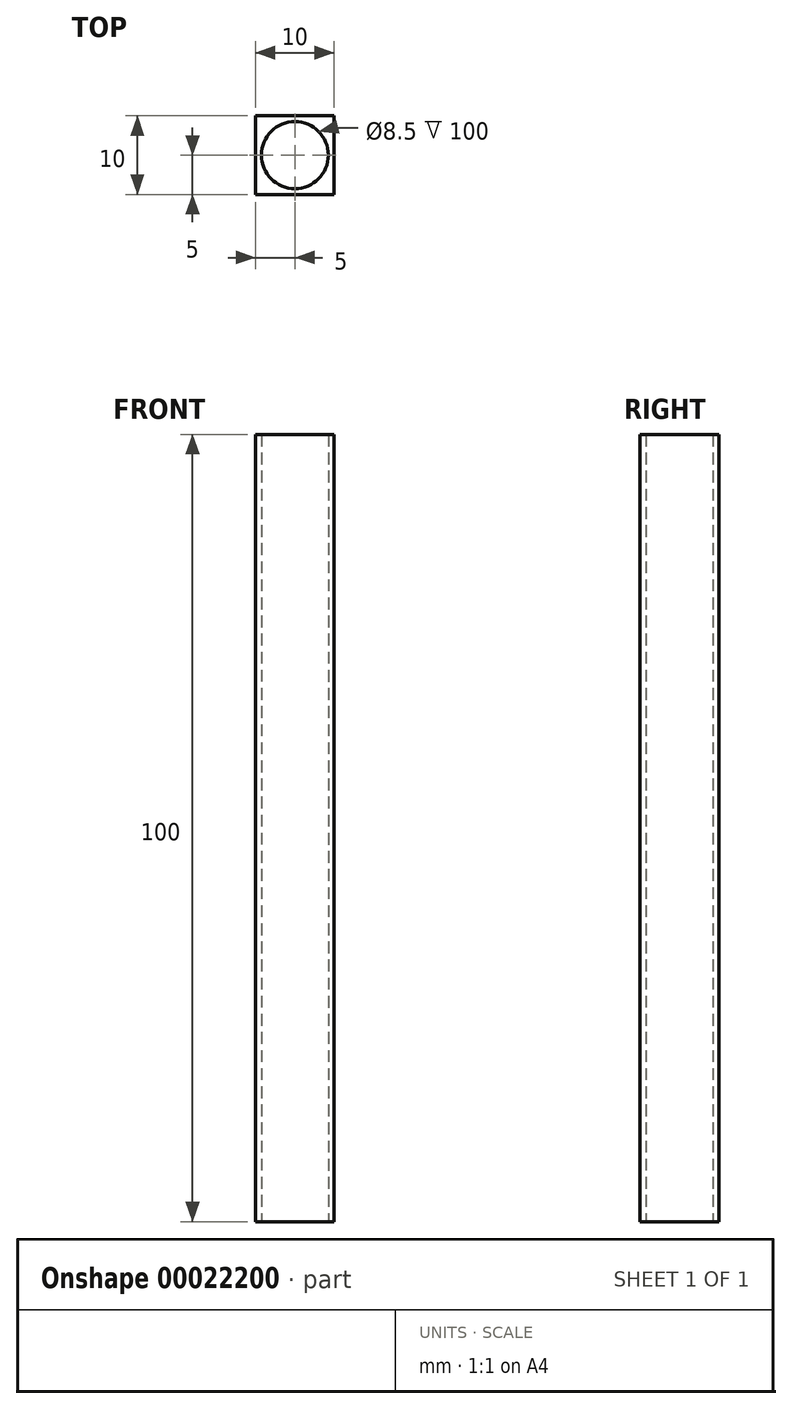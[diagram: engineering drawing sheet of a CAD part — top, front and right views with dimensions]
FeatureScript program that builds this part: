
annotation { "Feature Type Name" : "Feature", "Feature Type Description" : "" }
export const myFeature = defineFeature(function(context is Context, id is Id, definition is map)
    precondition{}
    {
        {
            var Q0;
            Q0=qCreatedBy(makeId("Top.planeOp"),FACE);
            var sketch = newSketch(context, id + "F0", { "sketchPlane" : qUnion([Q0])});
            skLineSegment(sketch, "E0.rect.bottom", {"start": v(4.5, -5) * mm, "end": v(-4.5, -5) * mm});
            skLineSegment(sketch, "E0.rect.top", {"start": v(4.5, 5) * mm, "end": v(-4.5, 5) * mm});
            skLineSegment(sketch, "E0.rect.left", {"start": v(5, -4.5) * mm, "end": v(5, 4.5) * mm});
            skLineSegment(sketch, "E0.rect.right", {"start": v(-5, -4.5) * mm, "end": v(-5, 4.5) * mm});
            skPoint(sketch, "E0.rect.middle", {"position": v(0, 0) * mm});
            skCircle(sketch, "E1", {"center": v(0, 0) * mm, "radius": 4.25 * mm});
            skPoint(sketch, "E2.visualSharp", {"position": v(-5, 5) * mm});
            skPoint(sketch, "E3.visualSharp", {"position": v(-5, -5) * mm});
            skPoint(sketch, "E4.visualSharp", {"position": v(5, -5) * mm});
            skPoint(sketch, "E5.visualSharp", {"position": v(5, 5) * mm});
            skLineSegment(sketch, "E6", {"start": v(-5, 5) * mm, "end": v(-5, 4.5) * mm});
            skLineSegment(sketch, "E7", {"start": v(-4.5, 5) * mm, "end": v(-5, 5) * mm});
            skLineSegment(sketch, "E8", {"start": v(4.5, 5) * mm, "end": v(5, 5) * mm});
            skLineSegment(sketch, "E9", {"start": v(5, 4.5) * mm, "end": v(5, 5) * mm});
            skLineSegment(sketch, "E10", {"start": v(5, -4.5) * mm, "end": v(5, -5) * mm});
            skLineSegment(sketch, "E11", {"start": v(4.5, -5) * mm, "end": v(5, -5) * mm});
            skLineSegment(sketch, "E12", {"start": v(-5, -4.5) * mm, "end": v(-5, -5) * mm});
            skLineSegment(sketch, "E13", {"start": v(-4.5, -5) * mm, "end": v(-5, -5) * mm});
            skSolve(sketch);
        }
        {
            var Q0;
            Q0=makeQuery(id+"F0.imprint","IMPRINT",FACE,{"disambiguationData":[TD([[makeQuery(id+"F0.imprint","IMPRINT",EDGE,{"derivedFrom":sQuery(id+"F0.wireOp",EDGE,"E0.rect.bottom")}),-1.0]])]});
            extrude(context, id + "F1", {"entities" : qUnion([Q0]), "depth" : 100 * mm});
        }
    });
